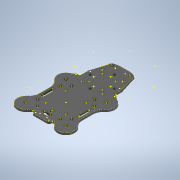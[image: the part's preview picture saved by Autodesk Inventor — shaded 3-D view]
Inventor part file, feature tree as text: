
AUTODESK INVENTOR PART (.ipt)
format: ipt  version: 2020 (Build 240168000, 168)  size: 577,024 bytes
history: native  units: in
note: dims shown in document units (in); Inventor stores cm internally (conversion verified against a paired STEP export)
features: sketch x6, projected_geometry x4, extrude x3
ambient origin geometry x8: Origin, YZ Plane, XZ Plane, XY Plane, X Axis, Y Axis, Z Axis, Center Point
bodies: Solid2 (feature_tree), Solid1 (feature_tree)
feature tree (13):
  extrude  "Extrusion1"  Depth=0.1772in
  sketch  "Sketch3"  dims[d20=0.1772in d21=0.1772in]
  sketch  "Sketch4"  dims[d22=0.1772in d23=0.1772in]
  sketch  "Sketch5"  dims[d24=0.1772in]
  extrude  "Extrusion2"  Depth=0.1772in
  extrude  "Extrusion3"  Depth=0.1772in
  sketch  "Sketch2"  dims[d18=0.1772in d19=0.1772in]
  projected_geometry  "Projected Loop2"
  projected_geometry  "Projected Loop3"
  projected_geometry  "Projected Loop4"
  projected_geometry  "Projected Loop5"
  sketch  "Sketch6"  dims[d25=0.1772in]
  sketch  "Sketch7"  dims[d26=0.1772in d27=0.1772in d28=0.1772in d29=0.1772in d30=0.1772in d31=0.1772in d32=0.1772in d33=0.3937in d34=0.0in d36=0.1772in d37=0.1772in d38=0.1772in d42=0.7092in d43=0.712in d44=0.7092in d45=0.7092in d46=0.3937in d47=0.0in d48=0.122in d49=0.122in d50=0.122in d51=0.122in d52=0.122in d53=1.0039in d54=1.0039in d55=1.0039in d56=1.0039in d57=1.4197in d58=0.3937in d59=0.0in]
